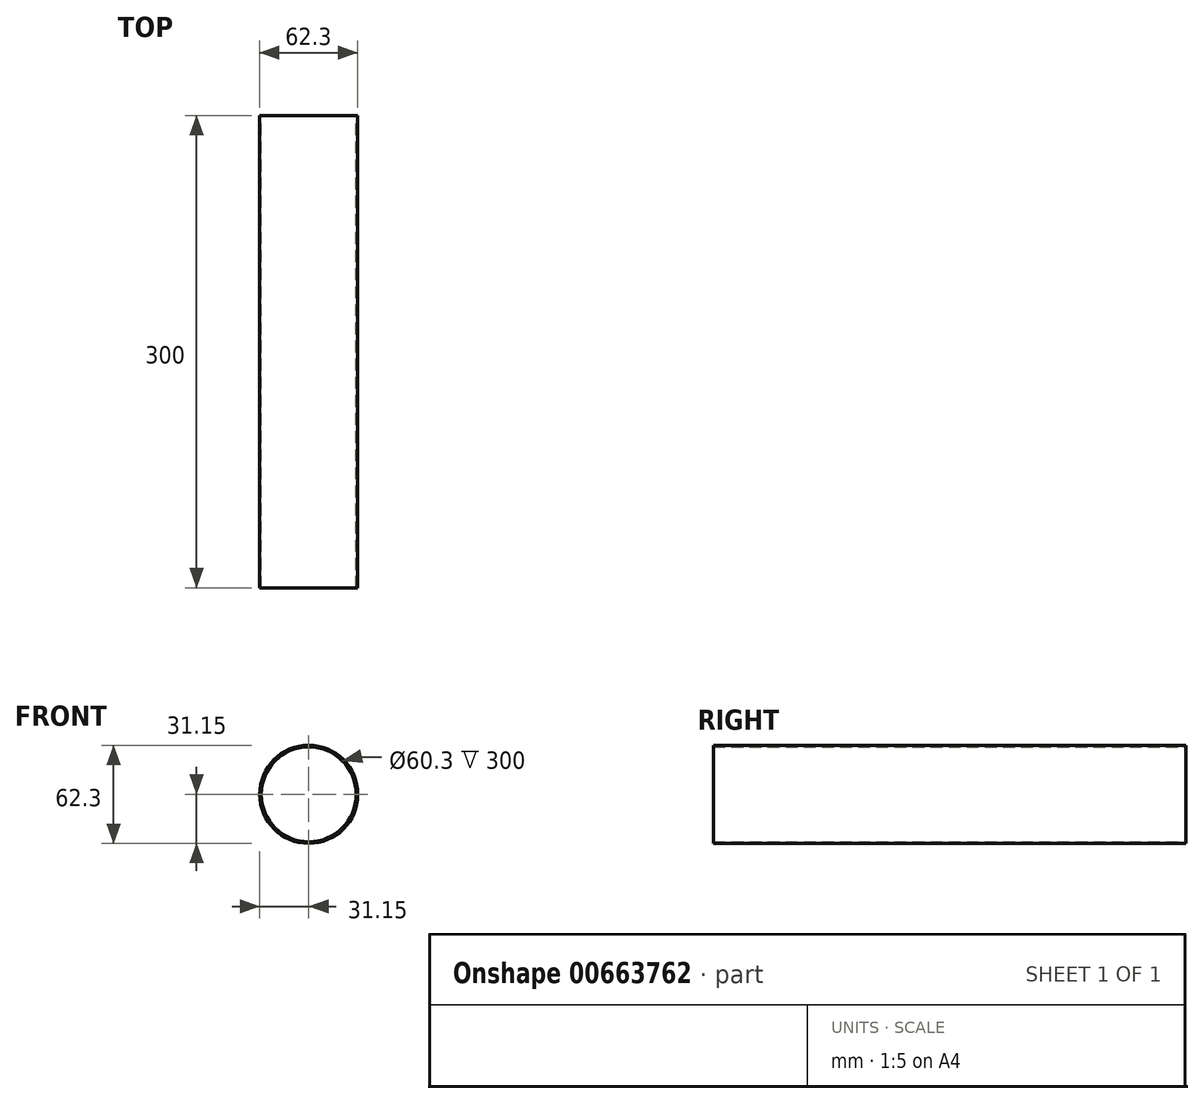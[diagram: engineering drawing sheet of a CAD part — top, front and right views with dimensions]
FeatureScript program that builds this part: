
annotation { "Feature Type Name" : "Feature", "Feature Type Description" : "" }
export const myFeature = defineFeature(function(context is Context, id is Id, definition is map)
    precondition{}
    {
        {
            var Q0;
            Q0=qCreatedBy(makeId("Front.planeOp"), FACE);
            var sketch = newSketch(context, id + "F0", { "sketchPlane" : qUnion([Q0])});
            skCircle(sketch, "E0", {"center": v(0, 0) * mm, "radius": 30.15 * mm});
            skCircle(sketch, "E1", {"center": v(0, 0) * mm, "radius": 31.15 * mm});
            skSolve(sketch);
        }
        {
            var Q0;
            Q0 = qSketchRegion(id + "F0", true);
            extrude(context, id + "F1", {"entities" : qUnion([Q0]), "depth" : 300 * mm, "offsetDistance" : 25 * mm});
        }
    });
